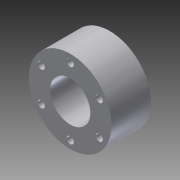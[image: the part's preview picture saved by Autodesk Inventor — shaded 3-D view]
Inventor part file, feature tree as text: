
AUTODESK INVENTOR PART (.ipt)
format: ipt  version: 2014 SP1 (Build 180222100, 222)  size: 139,264 bytes
history: native  units: in
note: dims shown in document units (in); Inventor stores cm internally (conversion verified against a paired STEP export)
features: extrude x1, sketch x1
ambient origin geometry x8: Origin, YZ Plane, XZ Plane, XY Plane, X Axis, Y Axis, Z Axis, Center Point
bodies: Solid1 (feature_tree)
feature tree (2):
  extrude  "Extrusion1"  [1 undecoded]
  sketch  "Sketch1"  dims[d0=1.106in d1=0.0in]
note: 1 required parameter value undecoded (feature->parameter linkage not recoverable at this tier; creation-order binding heuristic only, values carry confidence <= 0.55)
